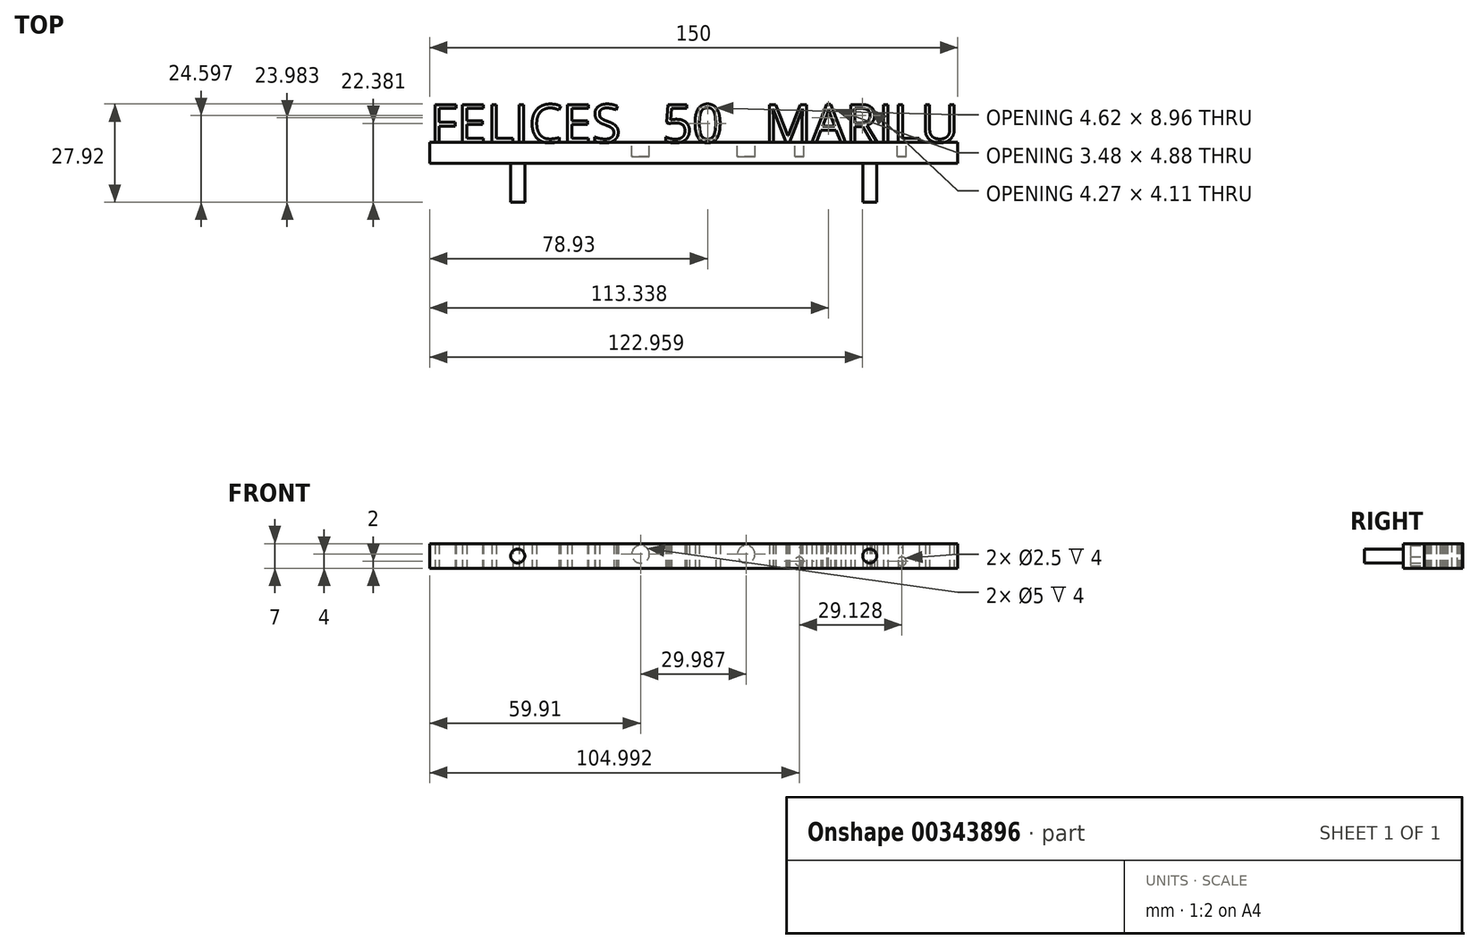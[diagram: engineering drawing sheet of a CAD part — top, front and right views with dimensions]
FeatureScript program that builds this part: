
annotation { "Feature Type Name" : "Feature", "Feature Type Description" : "" }
export const myFeature = defineFeature(function(context is Context, id is Id, definition is map)
    precondition{}
    {
        {
            var Q0;
            Q0=qCreatedBy(makeId("Top.planeOp"),FACE);
            var sketch = newSketch(context, id + "F0", { "sketchPlane" : qUnion([Q0])});
            skText(sketch, "E0", { "text": "FELICES   50   MARILU", "fontName": "OpenSans-Regular.ttf"});
            const initialGuessF0  = {"E0": [-0.15, 0, 1, 0, 0.01084]};
            skSetInitialGuess(sketch, initialGuessF0);
            skSolve(sketch);
        }
        {
            var Q0;
            Q0 = qSketchRegion(id + "F0", true);
            extrude(context, id + "F1", {"entities" : qUnion([Q0]), "depth" : 7 * mm});
        }
        {
            var Q0;
            Q0=qCreatedBy(makeId("Top.planeOp"),FACE);
            var sketch = newSketch(context, id + "F2", { "sketchPlane" : qUnion([Q0])});
            skLineSegment(sketch, "E1.bottom", {"start": v(0, 0) * mm, "end": v(-150, 0) * mm});
            skLineSegment(sketch, "E1.top", {"start": v(0, -6) * mm, "end": v(-150, -6) * mm});
            skLineSegment(sketch, "E1.left", {"start": v(0, 0) * mm, "end": v(0, -6) * mm});
            skLineSegment(sketch, "E1.right", {"start": v(-150, 0) * mm, "end": v(-150, -6) * mm});
            skSolve(sketch);
        }
        {
            var Q0;
            Q0 = qSketchRegion(id + "F2", true);
            extrude(context, id + "F3", {"entities" : qUnion([Q0]), "depth" : 7 * mm});
        }
        {
            var Q0;
            Q0=makeQuery(id+"F3.opExtrude","SWEPT_FACE",FACE,{"disambiguationData":[OSD([sQuery(id+"F2.wireOp",EDGE,"E1.bottom")])]});
            var sketch = newSketch(context, id + "F4", { "sketchPlane" : qUnion([Q0])});
            skLineSegment(sketch, "E2", {"start": v(45, 7) * mm, "end": v(45, 2) * mm});
            skCircle(sketch, "E3", {"center": v(45, 2) * mm, "radius": 1.25 * mm});
            skLineSegment(sketch, "E4", {"start": v(17.88, 7) * mm, "end": v(15.88, 7) * mm});
            skLineSegment(sketch, "E5", {"start": v(15.88, 7) * mm, "end": v(15.88, 2) * mm});
            skCircle(sketch, "E6", {"center": v(15.88, 2) * mm, "radius": 1.25 * mm});
            skLineSegment(sketch, "E7", {"start": v(96.6, 7) * mm, "end": v(90.1, 7) * mm});
            skLineSegment(sketch, "E8", {"start": v(90.1, 7) * mm, "end": v(90.1, 4) * mm});
            skCircle(sketch, "E9", {"center": v(90.1, 4) * mm, "radius": 2.5 * mm});
            skLineSegment(sketch, "E10", {"start": v(53.6, 7) * mm, "end": v(60.1, 7) * mm});
            skLineSegment(sketch, "E11", {"start": v(60.1, 7) * mm, "end": v(60.1, 4) * mm});
            skCircle(sketch, "E12", {"center": v(60.1, 4) * mm, "radius": 2.5 * mm});
            skSolve(sketch);
        }
        {
            var Q0;
            Q0 = qSketchRegion(id + "F4", true);
            extrude(context, id + "F5", {"entities" : qUnion([Q0]), "operationType" : NewBodyOperationType.REMOVE, "oppositeDirection" : true, "depth" : 4 * mm});
        }
        {
            var Q0;
            Q0=makeQuery(id+"F3.opExtrude","SWEPT_FACE",FACE,{"disambiguationData":[OSD([sQuery(id+"F2.wireOp",EDGE,"E1.top")])]});
            var sketch = newSketch(context, id + "F6", { "sketchPlane" : qUnion([Q0])});
            skLineSegment(sketch, "E13", {"start": v(-150, 3.5) * mm, "end": v(-125, 3.5) * mm});
            skPoint(sketch, "E13.endSnap0", {"position": v(0, 3.5) * mm});
            skLineSegment(sketch, "E14", {"start": v(0, 3.5) * mm, "end": v(-25, 3.5) * mm});
            skCircle(sketch, "E15", {"center": v(-125, 3.5) * mm, "radius": 2 * mm});
            skCircle(sketch, "E16", {"center": v(-25, 3.5) * mm, "radius": 2 * mm});
            skSolve(sketch);
        }
        {
            var Q0;
            Q0 = qSketchRegion(id + "F6", true);
            extrude(context, id + "F7", {"entities" : qUnion([Q0]), "operationType" : NewBodyOperationType.ADD, "depth" : 11 * mm});
        }
    });
